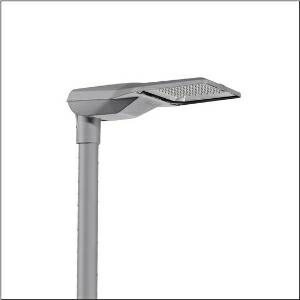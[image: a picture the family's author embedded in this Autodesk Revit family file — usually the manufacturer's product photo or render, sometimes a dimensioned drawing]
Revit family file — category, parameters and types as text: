
# Revit family: streetlight_sl_21_iq_midi___st0_8a_5xe3c41g08nb_9f8f
name_source: partatom
category: Lighting Fixtures
units: mm (PartAtom-declared; Revit-internal decimal feet)

## family parameters
Cut with Voids When Loaded = No
Host = Face
Light Source = No
Part Type = Normal
Room Calculation Point = No
Round Connector Dimension = Use Diameter
Shared = No

## types (1)
- --- (1 x LED, 24250 lm, 155.5 W, 4000K)
    Apparent Load = 155 VA
    CIE Flux Codes = 41 75 97 100 100
    Color Rendering = 70
    Color Temperature = 4000K
    Default Elevation = 1800 mm
    Description = Streetlight SL 21 iQ midi, mast luminaire, primary light control with lens, of PMMA, primary optical cover: cover, of toughened safety glass, transparent, light distribution: ST0.8a, light emission: direct distribution, primary light characteristic: asymmetric, installation type: post-top, side-entry, LED, High Power LED, rated luminous flux: 24.250lm, luminous efficacy: 156lm/W, light colour: 740, colour temperature: 4000K, control gear: iQ Street-Remote, control: Street-Remote, Auto-Match, Temp-Guard, Lumen-Switch, Night-Set, Smart-Wire, Light-Fading, Desk-Remote (wireless, voltage-free reading and setting of iQ features in the workshop via application-optimized NFC function/RFID function), optimised constant luminous flux control (CLO 2.0), pre-setting: linear dimming characteristic, mains connection: 230..240V, AC, 50/60Hz, start of lifetime: 156W, end of service life: 162W, reduction: 69W, luminaire housing, of diecast aluminium, powder-coated, SITECO metallic grey (DB 702S), corrosivity category C5 high according to DIN EN ISO 12944, please order mast flange separately, inclination adjustable: 0°, 5°, 10°, 15°, sealing non-destructively replaceable, multi-level sealing system, length: 644mm, width: 335mm, height: 110mm, mast flange for spigot size: 42mm (side-entry): 5XC10008XM4, 60/48mm (side-entry/post-top): 5XC10108XM2, 76/60mm (side-entry/post-top): 5XC10108XM1, mounting height: 4..8m, protection rating (complete): IP66, insulation class (complete): insulation class II (safety insulation), certification: CE, ENEC, ENEC+, VDE, impact resistance: IK10, permissible operating ambient temperature for outdoor applications: -40..+50°C, standard-compliant lighting for roads and squares, packaging unit: 1 piece

Light Distribution: ST0.8a
    Height = 111 mm
    Lamp = 1 x LED
    Lamp Light Flux = 24250 lm
    Lamp Power = 155.5 W
    Lamp count = 1
    Length = 644 mm
    Luminous efficacy = 156 lm/W
    Manufacturer = Siteco
    ModVariant = No
    Model = 5XE3C41G08NB
    Number of Poles = 1
    OnlyDefault = Yes
    Power Factor = 1
    Product Name = Streetlight SL 21 iQ midi | ST0.8a
    Product group = mast luminaire | pylon top
    ProductGroupID = 6100
    Protection Class = Protection class II
    Protection Degree = IP 66
    RLX_Detail_Level = 1
    RLX_Emergency_Light_Flux = 0 lm
    RLX_Emergency_Type = 0
    RLX_Emergency_Type_DB = No
    RlxData = <blob elided: 27153 chars, md5=b38e259d>
    Socket = socket
    Standby Power = 0 W
    System Light Flux = 24250 lm
    System Power = 155 W
    Type Comments = factory setting: luminous flux: 100 % | dim-lin: 254 | 823 mA
    Type Image = l_1004298.jpg
    URL = http://relux.com
    VarID = @adj_168353
    Voltage = 0 V
    Weight = 0.00 kg
    Width = 336 mm

## geometry (parser evidence)
native form markers: Blend x4, Sweep x11
no freeform markers — native parametric forms only
